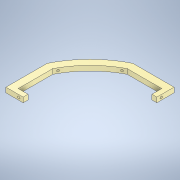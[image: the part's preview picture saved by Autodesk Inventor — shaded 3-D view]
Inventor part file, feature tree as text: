
AUTODESK INVENTOR PART (.ipt)
format: ipt  version: 2021 (Build 250183000, 183)  size: 184,832 bytes
history: native  units: in
note: dims shown in document units (in); Inventor stores cm internally (conversion verified against a paired STEP export)
features: other x5, sketch x5, hole x4, extrude x1, plane x1, split x1
ambient origin geometry x8: Origin, YZ Plane, XZ Plane, XY Plane, X Axis, Y Axis, Z Axis, Center Point
bodies: Solid1 (feature_tree)
feature tree (17):
  extrude  "Extrusion1"  Depth=0.0315in
  other  "radial plane for hole1"
  sketch  "sketch hole 1"  dims[d5=0.0315in d6=0.0315in]
  other  "radial plane for hole2"
  hole  "Hole2"  [1 undecoded]
  hole  "Hole1"  [1 undecoded]
  other  "tangential plane for hole3"
  other  "tangential plane for hole 4"
  other  "tangential plane for hole 5"
  sketch  "sketch hole 4"  dims[d14=3.4553in d15=0.3in]
  sketch  "Sketch8"  dims[d16=2.7553in d17=90.0deg d19=0.3in d20=2.7553in d21=0.7in d22=3.8553in d23=3.5553in d24=0.9252in d25=0.2in d26=0.0in d28=2.9301in d29=0.1in d30=2.9301in d31=0.1in d32=0.096in d33=0.75in d34=0.172in d35=0.25in d36=0.5635in d37=0.484in d38=0.8108in d39=0.096in d40=0.75in d41=0.172in d42=0.25in d43=0.5635in d44=0.484in d45=0.8108in d46=45.0deg d56=30.0deg d57=60.0deg d58=0.2in d59=0.1in d60=0.0in d61=0.2in d62=0.1in d63=0.0in d64=0.0849in d65=0.224in d66=0.375in d67=0.25in d68=0.5635in d69=0.349in d70=0.8108in d71=0.0849in d72=0.224in d73=0.375in d74=0.25in d75=0.5635in d76=0.349in d77=0.8108in d78=0.1in]
  hole  "Hole4"  [1 undecoded]
  hole  "Hole5"  [1 undecoded]
  plane  "Work Plane8"
  split  "Split1"
  sketch  "Sketch1"  dims[d7=90.0deg d8=0.2in]
  sketch  "sketch hole 2"  dims[d9=0.2in d13=90.0deg]
note: 4 required parameter values undecoded (feature->parameter linkage not recoverable at this tier; creation-order binding heuristic only, values carry confidence <= 0.55)
